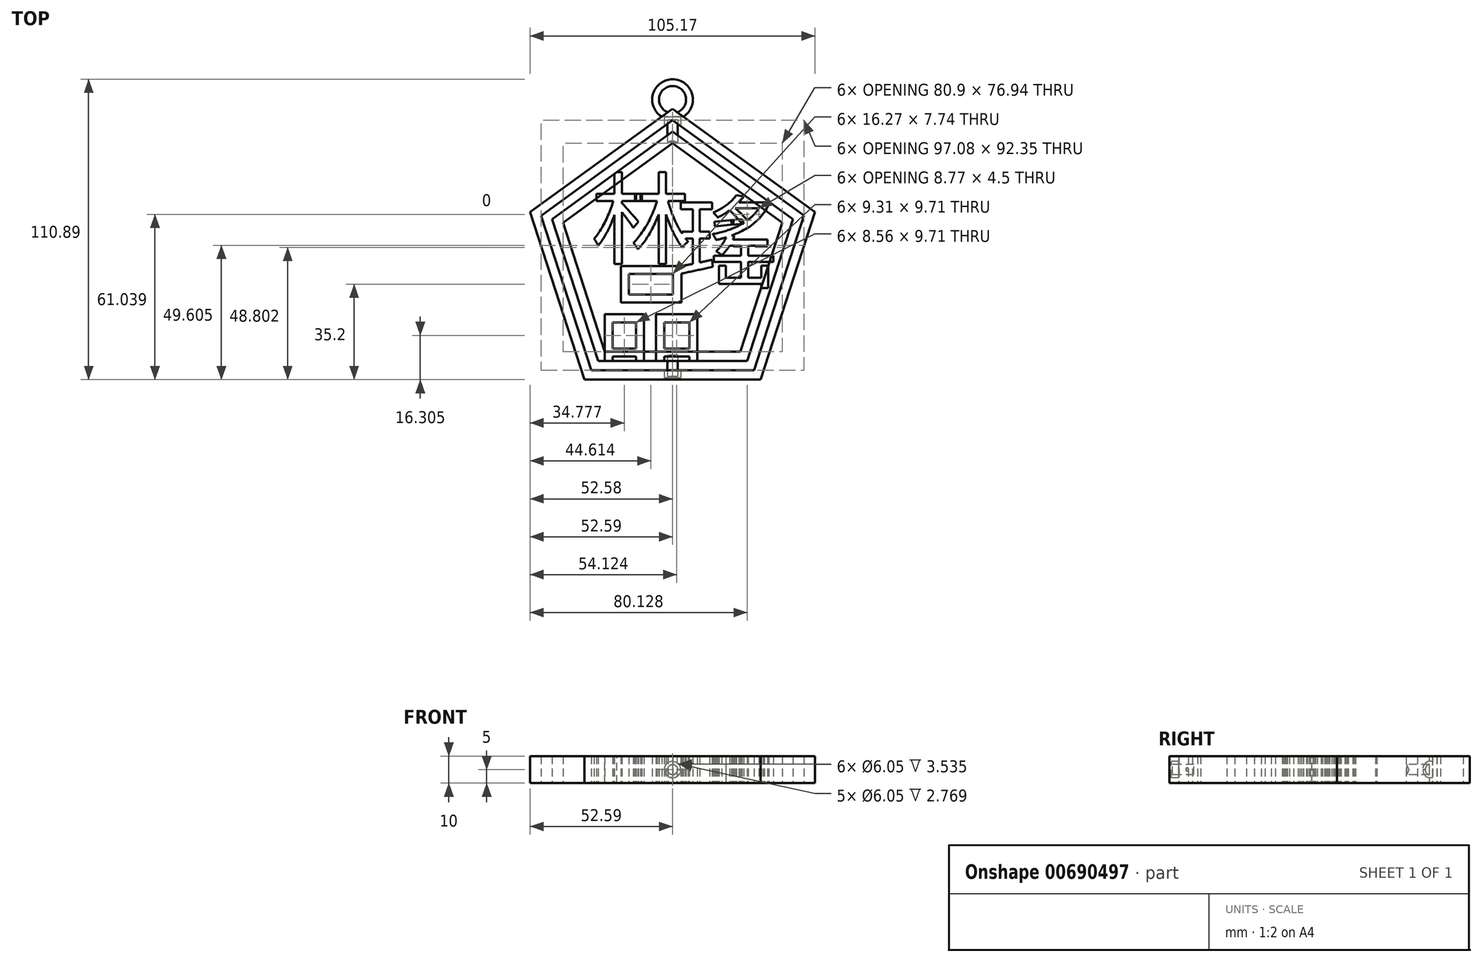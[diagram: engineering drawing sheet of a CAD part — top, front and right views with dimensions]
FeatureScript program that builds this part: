
annotation { "Feature Type Name" : "Feature", "Feature Type Description" : "" }
export const myFeature = defineFeature(function(context is Context, id is Id, definition is map)
    precondition{}
    {
        {
            var Q0;
            Q0=qCreatedBy(makeId("Top.planeOp"),FACE);
            var sketch = newSketch(context, id + "F0", { "sketchPlane" : qUnion([Q0])});
            skCircle(sketch, "E0.cCircle", {"center": v(0, 0) * mm, "radius": 42.53 * mm, "construction": true});
            skLineSegment(sketch, "E0.0", {"start": v(25, -34.4) * mm, "end": v(-25, -34.4) * mm});
            skLineSegment(sketch, "E0.1", {"start": v(-25, -34.4) * mm, "end": v(-40.45, 13.14) * mm});
            skLineSegment(sketch, "E0.2", {"start": v(-40.45, 13.14) * mm, "end": v(0, 42.53) * mm});
            skLineSegment(sketch, "E0.3", {"start": v(0, 42.53) * mm, "end": v(40.45, 13.14) * mm});
            skLineSegment(sketch, "E0.4", {"start": v(40.45, 13.14) * mm, "end": v(25, -34.4) * mm});
            skSolve(sketch);
        }
        {
            var Q0;
            Q0=makeQuery(id+"F0.imprint","IMPRINT",FACE,{"disambiguationData":[TD([[makeQuery(id+"F0.imprint","IMPRINT",EDGE,{"derivedFrom":sQuery(id+"F0.wireOp",EDGE,"E0.0")}),-1.0]])]});
            var sketch = newSketch(context, id + "F1", { "sketchPlane" : qUnion([Q0])});
            skCircle(sketch, "E1.cCircle", {"center": v(0, 0) * mm, "radius": 46.79 * mm, "construction": true});
            skLineSegment(sketch, "E1.0", {"start": v(44.5, 14.46) * mm, "end": v(27.5, -37.85) * mm});
            skLineSegment(sketch, "E1.1", {"start": v(27.5, -37.85) * mm, "end": v(-27.5, -37.85) * mm});
            skLineSegment(sketch, "E1.2", {"start": v(-27.5, -37.85) * mm, "end": v(-44.5, 14.46) * mm});
            skLineSegment(sketch, "E1.3", {"start": v(-44.5, 14.46) * mm, "end": v(0, 46.79) * mm});
            skLineSegment(sketch, "E1.4", {"start": v(0, 46.79) * mm, "end": v(44.5, 14.46) * mm});
            skSolve(sketch);
        }
        {
            var Q0;
            Q0=qCreatedBy(makeId("Top.planeOp"),FACE);
            var sketch = newSketch(context, id + "F2", { "sketchPlane" : qUnion([Q0])});
            skCircle(sketch, "E2.cCircle", {"center": v(0, 0) * mm, "radius": 51.04 * mm, "construction": true});
            skLineSegment(sketch, "E2.0", {"start": v(-0.03, 51.04) * mm, "end": v(48.53, 15.8) * mm});
            skLineSegment(sketch, "E2.1", {"start": v(48.53, 15.8) * mm, "end": v(30.03, -41.27) * mm});
            skLineSegment(sketch, "E2.2", {"start": v(30.03, -41.27) * mm, "end": v(-29.97, -41.3) * mm});
            skLineSegment(sketch, "E2.3", {"start": v(-29.97, -41.3) * mm, "end": v(-48.55, 15.74) * mm});
            skLineSegment(sketch, "E2.4", {"start": v(-48.55, 15.74) * mm, "end": v(-0.03, 51.04) * mm});
            skCircle(sketch, "E3.cCircle", {"center": v(0, 0) * mm, "radius": 55.3 * mm, "construction": true});
            skLineSegment(sketch, "E3.0", {"start": v(32.5, -44.73) * mm, "end": v(-32.5, -44.74) * mm});
            skLineSegment(sketch, "E3.1", {"start": v(-32.5, -44.74) * mm, "end": v(-52.59, 17.08) * mm});
            skLineSegment(sketch, "E3.2", {"start": v(-52.59, 17.08) * mm, "end": v(0, 55.3) * mm});
            skLineSegment(sketch, "E3.3", {"start": v(0, 55.3) * mm, "end": v(52.58, 17.1) * mm});
            skLineSegment(sketch, "E3.4", {"start": v(52.58, 17.1) * mm, "end": v(32.5, -44.73) * mm});
            skSolve(sketch);
        }
        {
            var Q0;
            Q0=qCreatedBy(makeId("Top.planeOp"),FACE);
            var sketch = newSketch(context, id + "F3", { "sketchPlane" : qUnion([Q0])});
            skText(sketch, "E4", { "text": "林", "fontName": "NotoSansCJKtc-Regular.otf"});
            skText(sketch, "E5", { "text": "品", "fontName": "NotoSansCJKtc-Regular.otf"});
            skText(sketch, "E6", { "text": "瑤", "fontName": "NotoSansCJKtc-Regular.otf"});
            const initialGuessF3  = {"E4": [-0.03018, 0.00073, 1, 0, 0.02675], "E5": [-0.02853, -0.0353, 1, 0, 0.02951], "E6": [0.00125, -0.008, 1, 0, 0.027]};
            skSetInitialGuess(sketch, initialGuessF3);
            skSolve(sketch);
        }
        {
            var Q0;
            Q0=qCreatedBy(makeId("Top.planeOp"),FACE);
            var sketch = newSketch(context, id + "F4", { "sketchPlane" : qUnion([Q0])});
            skLineSegment(sketch, "E7", {"start": v(21.76, 14.12) * mm, "end": v(25.6, 14.43) * mm});
            skLineSegment(sketch, "E8", {"start": v(21.76, 14.12) * mm, "end": v(21.86, 12.48) * mm});
            skLineSegment(sketch, "E9", {"start": v(21.86, 12.48) * mm, "end": v(26.31, 12.84) * mm});
            skLineSegment(sketch, "E10", {"start": v(26.31, 12.84) * mm, "end": v(25.6, 14.43) * mm});
            skLineSegment(sketch, "E11.bottom", {"start": v(-13.83, 23.87) * mm, "end": v(-11.29, 23.87) * mm});
            skLineSegment(sketch, "E11.top", {"start": v(-13.83, 21.24) * mm, "end": v(-11.29, 21.24) * mm});
            skLineSegment(sketch, "E11.left", {"start": v(-13.83, 23.87) * mm, "end": v(-13.83, 21.24) * mm});
            skLineSegment(sketch, "E11.right", {"start": v(-11.29, 23.87) * mm, "end": v(-11.29, 21.24) * mm});
            skSolve(sketch);
        }
        {
            var Q0;
            Q0=qCreatedBy(makeId("Top.planeOp"),FACE);
            var sketch = newSketch(context, id + "F5", { "sketchPlane" : qUnion([Q0])});
            skArc(sketch, "E12", {"start": v(3.94, 52.27) * mm, "mid": v(0.04, 66.15) * mm, "end": v(-4, 52.31) * mm});
            skArc(sketch, "E13", {"start": v(1.7, 53.95) * mm, "mid": v(0.03, 63.65) * mm, "end": v(-1.75, 53.97) * mm});
            skLineSegment(sketch, "E14", {"start": v(1.7, 53.95) * mm, "end": v(3.94, 52.27) * mm});
            skLineSegment(sketch, "E15", {"start": v(-4, 52.31) * mm, "end": v(-1.75, 53.97) * mm});
            skSolve(sketch);
        }
        {
            var Q0;
            Q0=qCreatedBy(makeId("Top.planeOp"),FACE);
            var sketch = newSketch(context, id + "F6", { "sketchPlane" : qUnion([Q0])});
            skLineSegment(sketch, "E16.bottom", {"start": v(1.86, 63.57) * mm, "end": v(-1.86, 63.57) * mm});
            skLineSegment(sketch, "E16.left", {"start": v(1.86, 51.17) * mm, "end": v(1.86, -43.58) * mm});
            skLineSegment(sketch, "E16.right", {"start": v(-1.86, 51.17) * mm, "end": v(-1.86, -43.58) * mm});
            skPoint(sketch, "E16.middle", {"position": v(0, 0) * mm});
            skLineSegment(sketch, "E17.bottom", {"start": v(3.03, 52.36) * mm, "end": v(-3.03, 52.36) * mm});
            skLineSegment(sketch, "E17.left", {"start": v(3.03, 52.36) * mm, "end": v(3.03, -44.06) * mm});
            skLineSegment(sketch, "E17.right", {"start": v(-3.03, 52.36) * mm, "end": v(-3.03, -44.06) * mm});
            skLineSegment(sketch, "E18", {"start": v(0, 52.36) * mm, "end": v(0, -43.58) * mm});
            skLineSegment(sketch, "E19", {"start": v(-3.03, 48.86) * mm, "end": v(-1.86, 49.7) * mm});
            skLineSegment(sketch, "E20", {"start": v(1.86, 49.67) * mm, "end": v(3.03, 48.82) * mm});
            skLineSegment(sketch, "E21", {"start": v(-3.03, -44.06) * mm, "end": v(3.03, -44.06) * mm});
            skLineSegment(sketch, "E22", {"start": v(-1.86, -43.58) * mm, "end": v(1.86, -43.58) * mm});
            skPoint(sketch, "E23.orphan", {"position": v(-1.86, -63.57) * mm});
            skPoint(sketch, "E24.orphan", {"position": v(-3.03, -52.36) * mm});
            skPoint(sketch, "E17.top.start.orphan", {"position": v(3.03, -52.36) * mm});
            skPoint(sketch, "E16.top.start.orphan", {"position": v(1.86, -63.57) * mm});
            skPoint(sketch, "E25.trimOffspring.end.orphan", {"position": v(0, -52.36) * mm});
            skLineSegment(sketch, "E26", {"start": v(-3.03, -41.3) * mm, "end": v(-1.86, -41.3) * mm});
            skLineSegment(sketch, "E27", {"start": v(3.03, -41.3) * mm, "end": v(1.86, -41.3) * mm});
            skLineSegment(sketch, "E28", {"start": v(0, -43.58) * mm, "end": v(0, -44.06) * mm});
            skLineSegment(sketch, "E29", {"start": v(-3.03, 42.32) * mm, "end": v(-1.86, 43) * mm});
            skLineSegment(sketch, "E30", {"start": v(-1.86, 43) * mm, "end": v(0, 43.58) * mm});
            skLineSegment(sketch, "E31", {"start": v(0, 43.58) * mm, "end": v(1.86, 42.87) * mm});
            skLineSegment(sketch, "E32", {"start": v(1.86, 42.87) * mm, "end": v(3.03, 42.08) * mm});
            skLineSegment(sketch, "E33", {"start": v(-3.03, -35.74) * mm, "end": v(-1.86, -35.74) * mm});
            skLineSegment(sketch, "E34", {"start": v(-1.86, -35.74) * mm, "end": v(0, -35.74) * mm});
            skLineSegment(sketch, "E35", {"start": v(0, -35.74) * mm, "end": v(1.86, -35.74) * mm});
            skLineSegment(sketch, "E36", {"start": v(1.86, -35.74) * mm, "end": v(3.03, -35.74) * mm});
            skLineSegment(sketch, "E37", {"start": v(-1.86, 51.17) * mm, "end": v(1.86, 51.17) * mm});
            skSolve(sketch);
        }
        {
            var Q0;
            {var subQ0=sQuery(id+"F6.wireOp",EDGE,"E16.left");Q0=makeQuery(id+"F6.imprint","IMPRINT",FACE,{"disambiguationData":[TD([[makeQuery(id+"F6.imprint","IMPRINT",EDGE,{"derivedFrom":subQ0}),-1.0]])]});}
            var Q1;
            Q1=sQuery(id+"F6.wireOp",EDGE,"E18");
            revolve(context, id + "F7", {"surfaceOperationType" : NewSurfaceOperationType.NEW, "entities" : qUnion([Q0]), "axis" : qUnion([Q1]), "revolveType" : RevolveType.FULL, "oppositeDirection" : true});
        }
        {
            var Q0;
            Q0=makeQuery(id+"F2.imprint","IMPRINT",FACE,{"disambiguationData":[TD([[makeQuery(id+"F2.imprint","IMPRINT",EDGE,{"derivedFrom":sQuery(id+"F2.wireOp",EDGE,"E2.0")}),1.0]])]});
            var Q1;
            Q1=makeQuery(id+"F5.imprint","IMPRINT",FACE,{"disambiguationData":[TD([[makeQuery(id+"F5.imprint","IMPRINT",EDGE,{"derivedFrom":sQuery(id+"F5.wireOp",EDGE,"E12")}),1.0]])]});
            var Q2;
            Q2=makeQuery(id+"F1.imprint","IMPRINT",FACE,{"disambiguationData":[TD([[makeQuery(id+"F1.imprint","IMPRINT",EDGE,{"derivedFrom":sQuery(id+"F1.wireOp",EDGE,"E1.0")}),-1.0]])]});
            var Q3;
            Q3 = qSketchRegion(id + "F3", true);
            var Q4;
            Q4 = qSketchRegion(id + "F4", true);
            extrude(context, id + "F8", {"entities" : qUnion([Q0, Q1, Q2, Q3, Q4]), "depth" : 5 * mm, "offsetDistance" : 25 * mm, "hasSecondDirection" : true, "secondDirectionOppositeDirection" : true, "secondDirectionDepth" : 5 * mm});
        }
        {
            var Q0;
            Q0=makeQuery(id+"F8.opExtrude","CAP_FACE",FACE,{"disambiguationData":[OSD([sQuery(id+"F0.wireOp",EDGE,"E0.0"),sQuery(id+"F0.wireOp",EDGE,"E0.1"),sQuery(id+"F0.wireOp",EDGE,"E0.2"),sQuery(id+"F0.wireOp",EDGE,"E0.3"),sQuery(id+"F0.wireOp",EDGE,"E0.4"),sQuery(id+"F1.wireOp",EDGE,"E1.0"),sQuery(id+"F1.wireOp",EDGE,"E1.1"),sQuery(id+"F1.wireOp",EDGE,"E1.2"),sQuery(id+"F1.wireOp",EDGE,"E1.3"),sQuery(id+"F1.wireOp",EDGE,"E1.4")])],"isStart":false});
            var sketch = newSketch(context, id + "F9", { "sketchPlane" : qUnion([Q0])});
            skLineSegment(sketch, "E38", {"start": v(-21.61, 31.08) * mm, "end": v(-18.2, 33.56) * mm});
            skLineSegment(sketch, "E39", {"start": v(-18.2, 33.56) * mm, "end": v(-18.2, 34.43) * mm});
            skLineSegment(sketch, "E40", {"start": v(-18.2, 34.43) * mm, "end": v(-21.64, 34.43) * mm});
            skLineSegment(sketch, "E41", {"start": v(-21.64, 34.43) * mm, "end": v(-21.61, 31.08) * mm});
            skLineSegment(sketch, "E42", {"start": v(31.95, 23.58) * mm, "end": v(32.24, 23.62) * mm});
            skLineSegment(sketch, "E43", {"start": v(32.24, 23.62) * mm, "end": v(33.77, 22.91) * mm});
            skLineSegment(sketch, "E44", {"start": v(33.77, 22.91) * mm, "end": v(33.5, 22.44) * mm});
            skLineSegment(sketch, "E45", {"start": v(33.5, 22.44) * mm, "end": v(31.95, 23.58) * mm});
            skLineSegment(sketch, "E46", {"start": v(-13.78, -37.85) * mm, "end": v(-13.78, -38.1) * mm});
            skLineSegment(sketch, "E47", {"start": v(-13.78, -38.1) * mm, "end": v(-9.15, -38.1) * mm});
            skLineSegment(sketch, "E48", {"start": v(-13.78, -37.85) * mm, "end": v(-9.15, -37.85) * mm});
            skLineSegment(sketch, "E49", {"start": v(-9.15, -37.85) * mm, "end": v(-9.15, -38.1) * mm});
            skLineSegment(sketch, "E50", {"start": v(-25.14, -37.85) * mm, "end": v(-25.14, -38.46) * mm});
            skLineSegment(sketch, "E51", {"start": v(-25.14, -38.46) * mm, "end": v(-20.72, -38.46) * mm});
            skLineSegment(sketch, "E52", {"start": v(-20.72, -38.46) * mm, "end": v(-20.72, -37.85) * mm});
            skLineSegment(sketch, "E53", {"start": v(-20.72, -37.85) * mm, "end": v(-25.14, -37.85) * mm});
            skLineSegment(sketch, "E54.bottom", {"start": v(-6.58, -37.85) * mm, "end": v(-1.74, -37.85) * mm});
            skLineSegment(sketch, "E54.top", {"start": v(-6.58, -38.53) * mm, "end": v(-1.74, -38.53) * mm});
            skLineSegment(sketch, "E54.left", {"start": v(-6.58, -37.85) * mm, "end": v(-6.58, -38.53) * mm});
            skLineSegment(sketch, "E54.right", {"start": v(-1.74, -37.85) * mm, "end": v(-1.74, -38.53) * mm});
            skLineSegment(sketch, "E55.bottom", {"start": v(5.52, -37.85) * mm, "end": v(10.55, -37.85) * mm});
            skLineSegment(sketch, "E55.top", {"start": v(5.52, -38.55) * mm, "end": v(10.55, -38.55) * mm});
            skLineSegment(sketch, "E55.left", {"start": v(5.52, -37.85) * mm, "end": v(5.52, -38.55) * mm});
            skLineSegment(sketch, "E55.right", {"start": v(10.55, -37.85) * mm, "end": v(10.55, -38.55) * mm});
            skSolve(sketch);
        }
        {
            var Q0;
            Q0 = qSketchRegion(id + "F9", true);
            var Q1;
            Q1 = qSketchRegion(id + "Fck8w4hx1lNFMyH_9", true);
            extrude(context, id + "F10", {"entities" : qUnion([Q0, Q1]), "operationType" : NewBodyOperationType.REMOVE, "oppositeDirection" : true, "depth" : 10 * mm, "offsetDistance" : 25 * mm});
        }
        {
            var Q0;
            {var subQ3=sQuery(id+"F6.wireOp",EDGE,"E20");Q0=makeQuery(id+"F6.imprint","IMPRINT",FACE,{"disambiguationData":[TD([[makeQuery(id+"F6.imprint","IMPRINT",EDGE,{"derivedFrom":subQ3}),1.0]])]});}
            var Q1;
            {var subQ7=sQuery(id+"F6.wireOp",EDGE,"E27");Q1=makeQuery(id+"F6.imprint","IMPRINT",FACE,{"disambiguationData":[TD([[makeQuery(id+"F6.imprint","IMPRINT",EDGE,{"derivedFrom":subQ7}),1.0]])]});}
            var Q2;
            Q2=sQuery(id+"F6.wireOp",EDGE,"E18");
            revolve(context, id + "F11", {"operationType" : NewBodyOperationType.REMOVE, "surfaceOperationType" : NewSurfaceOperationType.NEW, "entities" : qUnion([Q0, Q1]), "axis" : qUnion([Q2]), "revolveType" : RevolveType.FULL, "oppositeDirection" : true});
        }
    });
